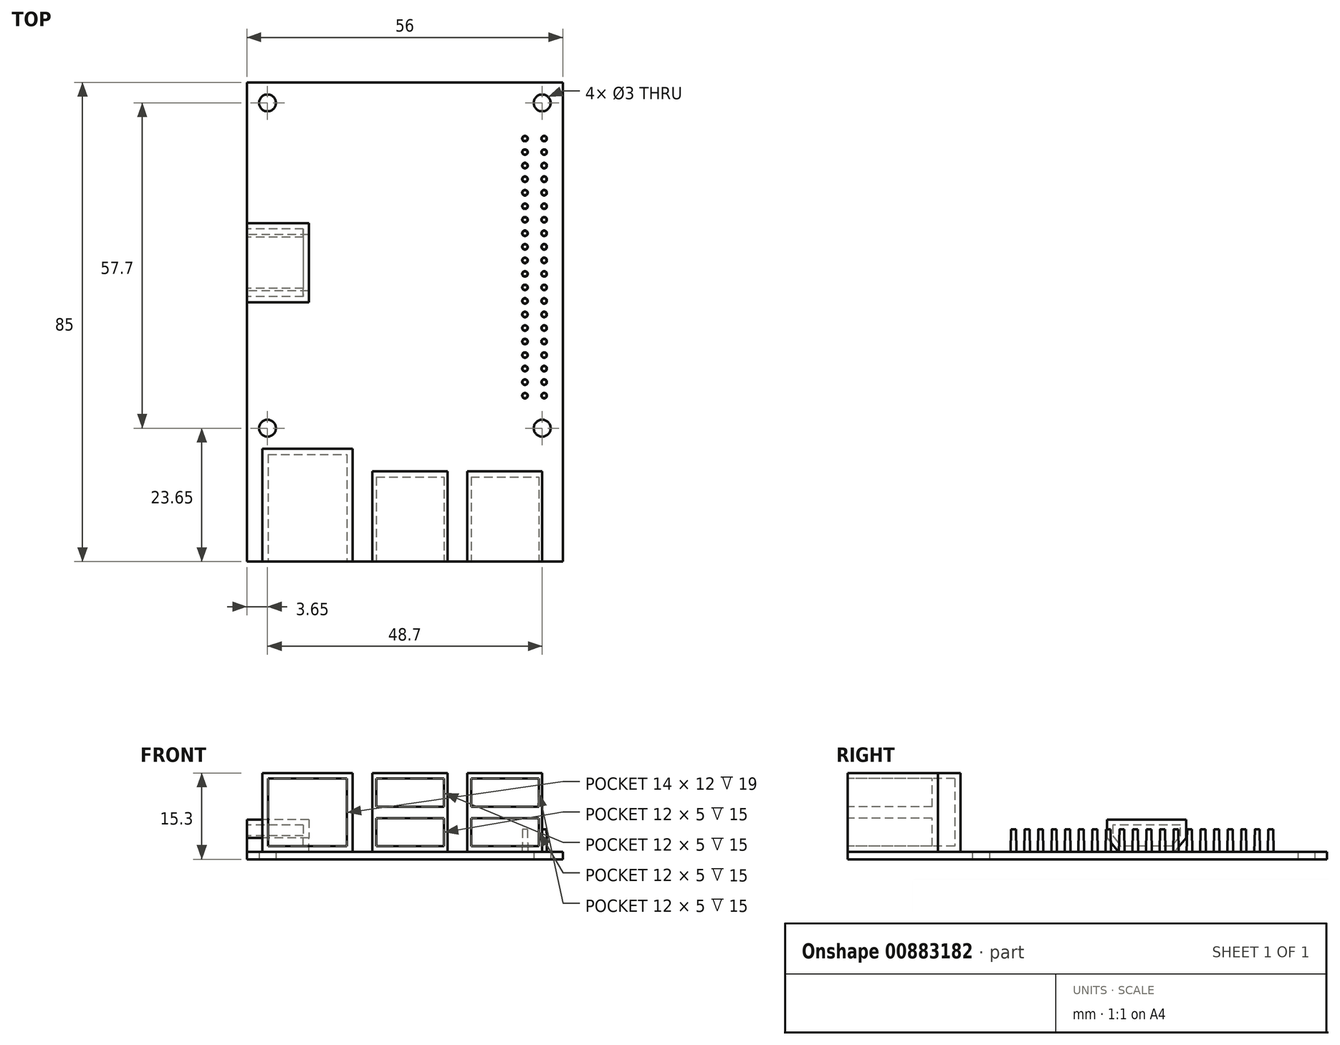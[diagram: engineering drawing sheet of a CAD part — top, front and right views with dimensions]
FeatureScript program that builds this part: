
annotation { "Feature Type Name" : "Feature", "Feature Type Description" : "" }
export const myFeature = defineFeature(function(context is Context, id is Id, definition is map)
    precondition{}
    {
        {
            var Q0;
            Q0=qCreatedBy(makeId("Top.planeOp"),FACE);
            var sketch = newSketch(context, id + "F0", { "sketchPlane" : qUnion([Q0])});
            skLineSegment(sketch, "E0.bottom", {"start": v(-28, 42.5) * mm, "end": v(28, 42.5) * mm});
            skLineSegment(sketch, "E0.top", {"start": v(-28, -42.5) * mm, "end": v(28, -42.5) * mm});
            skLineSegment(sketch, "E0.left", {"start": v(-28, 42.5) * mm, "end": v(-28, -42.5) * mm});
            skLineSegment(sketch, "E0.right", {"start": v(28, 42.5) * mm, "end": v(28, -42.5) * mm});
            skPoint(sketch, "E0.middle", {"position": v(0, 0) * mm});
            skCircle(sketch, "E1", {"center": v(-24.35, 38.85) * mm, "radius": 1.5 * mm});
            skCircle(sketch, "E2", {"center": v(-24.35, -18.85) * mm, "radius": 1.5 * mm});
            skCircle(sketch, "E3.MirrorC", {"center": v(24.35, 38.85) * mm, "radius": 1.5 * mm});
            skCircle(sketch, "E4.MirrorC", {"center": v(24.35, -18.85) * mm, "radius": 1.5 * mm});
            skSolve(sketch);
        }
        {
            var Q0;
            Q0=makeQuery(id+"F0.imprint","IMPRINT",FACE,{"disambiguationData":[TD([[makeQuery(id+"F0.imprint","IMPRINT",EDGE,{"derivedFrom":sQuery(id+"F0.wireOp",EDGE,"E0.bottom")}),-1.0]])]});
            extrude(context, id + "F1", {"entities" : qUnion([Q0]), "depth" : 1.3 * mm, "offsetDistance" : 25 * mm});
        }
        {
            var Q0;
            Q0=makeQuery(id+"F1.opExtrude","CAP_FACE",FACE,{"disambiguationData":[OSD([sQuery(id+"F0.wireOp",EDGE,"E0.bottom"),sQuery(id+"F0.wireOp",EDGE,"E0.top"),sQuery(id+"F0.wireOp",EDGE,"E0.left"),sQuery(id+"F0.wireOp",EDGE,"E0.right"),sQuery(id+"F0.wireOp",EDGE,"E1"),sQuery(id+"F0.wireOp",EDGE,"E2"),sQuery(id+"F0.wireOp",EDGE,"E3.MirrorC"),sQuery(id+"F0.wireOp",EDGE,"E4.MirrorC")])],"isStart":false});
            var sketch = newSketch(context, id + "F2", { "sketchPlane" : qUnion([Q0])});
            skLineSegment(sketch, "E5.bottom", {"start": v(-25.25, -22.5) * mm, "end": v(-9.25, -22.5) * mm});
            skLineSegment(sketch, "E5.top", {"start": v(-25.25, -43.8) * mm, "end": v(-9.25, -43.8) * mm});
            skLineSegment(sketch, "E5.left", {"start": v(-25.25, -22.5) * mm, "end": v(-25.25, -43.8) * mm});
            skLineSegment(sketch, "E5.right", {"start": v(-9.25, -22.5) * mm, "end": v(-9.25, -43.8) * mm});
            skLineSegment(sketch, "E6.bottom", {"start": v(-5.75, -26.5) * mm, "end": v(7.55, -26.5) * mm});
            skLineSegment(sketch, "E6.top", {"start": v(-5.75, -43.8) * mm, "end": v(7.55, -43.8) * mm});
            skLineSegment(sketch, "E6.left", {"start": v(-5.75, -26.5) * mm, "end": v(-5.75, -43.8) * mm});
            skLineSegment(sketch, "E6.right", {"start": v(7.55, -26.5) * mm, "end": v(7.55, -43.8) * mm});
            skLineSegment(sketch, "E7.bottom", {"start": v(11.05, -26.5) * mm, "end": v(24.35, -26.5) * mm});
            skLineSegment(sketch, "E7.top", {"start": v(11.05, -43.8) * mm, "end": v(24.35, -43.8) * mm});
            skLineSegment(sketch, "E7.left", {"start": v(11.05, -26.5) * mm, "end": v(11.05, -43.8) * mm});
            skLineSegment(sketch, "E7.right", {"start": v(24.35, -26.5) * mm, "end": v(24.35, -43.8) * mm});
            skSolve(sketch);
        }
        {
            var Q0;
            {var subQ0=sQuery(id+"F2.wireOp",EDGE,"E5.bottom");Q0=makeQuery(id+"F2.imprint","IMPRINT",FACE,{"disambiguationData":[TD([[makeQuery(id+"F2.imprint","IMPRINT",EDGE,{"derivedFrom":subQ0}),-1.0]])]});}
            var Q1;
            {var subQ0=sQuery(id+"F2.wireOp",EDGE,"E6.bottom");Q1=makeQuery(id+"F2.imprint","IMPRINT",FACE,{"disambiguationData":[TD([[makeQuery(id+"F2.imprint","IMPRINT",EDGE,{"derivedFrom":subQ0}),-1.0]])]});}
            var Q2;
            {var subQ0=sQuery(id+"F2.wireOp",EDGE,"E7.bottom");Q2=makeQuery(id+"F2.imprint","IMPRINT",FACE,{"disambiguationData":[TD([[makeQuery(id+"F2.imprint","IMPRINT",EDGE,{"derivedFrom":subQ0}),-1.0]])]});}
            extrude(context, id + "F3", {"entities" : qUnion([Q0, Q1, Q2]), "depth" : 14 * mm, "offsetDistance" : 25 * mm});
        }
        {
            var Q0;
            {var subQ0=sQuery(id+"F0.wireOp",EDGE,"E0.top");var subQ1=makeQuery(id+"F1.opExtrude","CAP_EDGE",EDGE,{"disambiguationData":[OSD([subQ0])],"isStart":false});Q0=makeQuery(id+"F3.opExtrude","SWEPT_FACE",FACE,{"disambiguationData":[OSD([subQ0]),TDD([makeQuery(id+"F2.imprint","IMPRINT",EDGE,{"disambiguationData":[TD([[makeQuery(id+"F2.imprint","INTERSECT",VERTEX,{"derivedFrom":[subQ1,sQuery(id+"F2.wireOp",EDGE,"E5.left")]}),-1.0]])],"derivedFrom":subQ1})])]});}
            shell(context, id + "F4", {"entities" : qUnion([Q0]), "thickness" : 1 * mm});
        }
        {
            var Q0;
            {var subQ0=sQuery(id+"F0.wireOp",EDGE,"E0.top");var subQ1=makeQuery(id+"F1.opExtrude","CAP_EDGE",EDGE,{"disambiguationData":[OSD([subQ0])],"isStart":false});Q0=makeQuery(id+"F3.opExtrude","SWEPT_FACE",FACE,{"disambiguationData":[OSD([subQ0]),TDD([makeQuery(id+"F2.imprint","IMPRINT",EDGE,{"disambiguationData":[TD([[makeQuery(id+"F2.imprint","INTERSECT",VERTEX,{"derivedFrom":[subQ1,sQuery(id+"F2.wireOp",EDGE,"E6.left")]}),-1.0]])],"derivedFrom":subQ1})])]});}
            var sketch = newSketch(context, id + "F5", { "sketchPlane" : qUnion([Q0])});
            skLineSegment(sketch, "E8.bottom", {"start": v(-5.05, 9.3) * mm, "end": v(6.95, 9.3) * mm});
            skLineSegment(sketch, "E8.top", {"start": v(-5.05, 14.3) * mm, "end": v(6.95, 14.3) * mm});
            skLineSegment(sketch, "E8.left", {"start": v(-5.05, 9.3) * mm, "end": v(-5.05, 14.3) * mm});
            skLineSegment(sketch, "E8.right", {"start": v(6.95, 9.3) * mm, "end": v(6.95, 14.3) * mm});
            skLineSegment(sketch, "E9.bottom", {"start": v(-5.05, 2.3) * mm, "end": v(6.95, 2.3) * mm});
            skLineSegment(sketch, "E9.top", {"start": v(-5.05, 7.3) * mm, "end": v(6.95, 7.3) * mm});
            skLineSegment(sketch, "E9.left", {"start": v(-5.05, 2.3) * mm, "end": v(-5.05, 7.3) * mm});
            skLineSegment(sketch, "E9.right", {"start": v(6.95, 2.3) * mm, "end": v(6.95, 7.3) * mm});
            skLineSegment(sketch, "E10.bottom", {"start": v(11.75, 9.3) * mm, "end": v(23.75, 9.3) * mm});
            skLineSegment(sketch, "E10.top", {"start": v(11.75, 14.3) * mm, "end": v(23.75, 14.3) * mm});
            skLineSegment(sketch, "E10.left", {"start": v(11.75, 9.3) * mm, "end": v(11.75, 14.3) * mm});
            skLineSegment(sketch, "E10.right", {"start": v(23.75, 9.3) * mm, "end": v(23.75, 14.3) * mm});
            skLineSegment(sketch, "E11.bottom", {"start": v(11.75, 2.3) * mm, "end": v(23.75, 2.3) * mm});
            skLineSegment(sketch, "E11.top", {"start": v(11.75, 7.3) * mm, "end": v(23.75, 7.3) * mm});
            skLineSegment(sketch, "E11.left", {"start": v(11.75, 2.3) * mm, "end": v(11.75, 7.3) * mm});
            skLineSegment(sketch, "E11.right", {"start": v(23.75, 2.3) * mm, "end": v(23.75, 7.3) * mm});
            skSolve(sketch);
        }
        {
            var Q0;
            Q0 = qSketchRegion(id + "F5", true);
            extrude(context, id + "F6", {"entities" : qUnion([Q0]), "operationType" : NewBodyOperationType.REMOVE, "endBound" : BoundingType.UP_TO_NEXT, "oppositeDirection" : true, "depth" : 25 * mm, "hasOffset" : true, "offsetDistance" : 1 * mm});
        }
        {
            var Q0;
            Q0=makeQuery(id+"F1.opExtrude","SWEPT_FACE",FACE,{"disambiguationData":[OSD([sQuery(id+"F0.wireOp",EDGE,"E0.left")])]});
            var sketch = newSketch(context, id + "F7", { "sketchPlane" : qUnion([Q0])});
            skLineSegment(sketch, "E12", {"start": v(-15.5, 1.3) * mm, "end": v(-17.5, 3.8) * mm});
            skLineSegment(sketch, "E13", {"start": v(-17.5, 3.8) * mm, "end": v(-17.5, 7.05) * mm});
            skLineSegment(sketch, "E14", {"start": v(-17.5, 7.05) * mm, "end": v(-3.5, 7.05) * mm});
            skLineSegment(sketch, "E15", {"start": v(-3.5, 7.05) * mm, "end": v(-3.5, 3.8) * mm});
            skLineSegment(sketch, "E16", {"start": v(-3.5, 3.8) * mm, "end": v(-5.5, 1.3) * mm});
            skLineSegment(sketch, "E17", {"start": v(-5.5, 1.3) * mm, "end": v(-15.5, 1.3) * mm});
            skSolve(sketch);
        }
        {
            var Q0;
            Q0=makeQuery(id+"F7.imprint","IMPRINT",FACE,{"disambiguationData":[TD([[makeQuery(id+"F7.imprint","IMPRINT",EDGE,{"derivedFrom":sQuery(id+"F7.wireOp",EDGE,"E12")}),-1.0]])]});
            extrude(context, id + "F8", {"entities" : qUnion([Q0]), "oppositeDirection" : true, "depth" : 11 * mm, "offsetDistance" : 25 * mm});
        }
        {
            var Q0;
            Q0=makeQuery(id+"F8.opExtrude","CAP_FACE",FACE,{"disambiguationData":[OSD([sQuery(id+"F7.wireOp",EDGE,"E12"),sQuery(id+"F7.wireOp",EDGE,"E13"),sQuery(id+"F7.wireOp",EDGE,"E14"),sQuery(id+"F7.wireOp",EDGE,"E15"),sQuery(id+"F7.wireOp",EDGE,"E16"),sQuery(id+"F7.wireOp",EDGE,"E17")])],"isStart":true});
            shell(context, id + "F9", {"entities" : qUnion([Q0]), "thickness" : 1 * mm});
        }
        {
            var Q0;
            Q0=makeQuery(id+"F1.opExtrude","CAP_FACE",FACE,{"disambiguationData":[OSD([sQuery(id+"F0.wireOp",EDGE,"E0.bottom"),sQuery(id+"F0.wireOp",EDGE,"E0.top"),sQuery(id+"F0.wireOp",EDGE,"E0.left"),sQuery(id+"F0.wireOp",EDGE,"E0.right"),sQuery(id+"F0.wireOp",EDGE,"E1"),sQuery(id+"F0.wireOp",EDGE,"E2"),sQuery(id+"F0.wireOp",EDGE,"E3.MirrorC"),sQuery(id+"F0.wireOp",EDGE,"E4.MirrorC")])],"isStart":false});
            var sketch = newSketch(context, id + "F10", { "sketchPlane" : qUnion([Q0])});
            skCircle(sketch, "E18", {"center": v(21.3, 32.52) * mm, "radius": 0.5 * mm});
            skCircle(sketch, "E19.0.1.0", {"center": v(21.3, 30.12) * mm, "radius": 0.5 * mm});
            skCircle(sketch, "E19.0.2.0", {"center": v(21.3, 27.72) * mm, "radius": 0.5 * mm});
            skCircle(sketch, "E19.0.3.0", {"center": v(21.3, 25.32) * mm, "radius": 0.5 * mm});
            skCircle(sketch, "E19.0.4.0", {"center": v(21.3, 22.92) * mm, "radius": 0.5 * mm});
            skCircle(sketch, "E19.0.5.0", {"center": v(21.3, 20.52) * mm, "radius": 0.5 * mm});
            skCircle(sketch, "E19.0.6.0", {"center": v(21.3, 18.12) * mm, "radius": 0.5 * mm});
            skCircle(sketch, "E19.0.7.0", {"center": v(21.3, 15.72) * mm, "radius": 0.5 * mm});
            skCircle(sketch, "E19.0.8.0", {"center": v(21.3, 13.32) * mm, "radius": 0.5 * mm});
            skCircle(sketch, "E19.0.9.0", {"center": v(21.3, 10.92) * mm, "radius": 0.5 * mm});
            skCircle(sketch, "E19.0.10.0", {"center": v(21.3, 8.52) * mm, "radius": 0.5 * mm});
            skCircle(sketch, "E19.0.11.0", {"center": v(21.3, 6.12) * mm, "radius": 0.5 * mm});
            skCircle(sketch, "E19.0.12.0", {"center": v(21.3, 3.72) * mm, "radius": 0.5 * mm});
            skCircle(sketch, "E19.0.13.0", {"center": v(21.3, 1.32) * mm, "radius": 0.5 * mm});
            skCircle(sketch, "E19.0.14.0", {"center": v(21.3, -1.08) * mm, "radius": 0.5 * mm});
            skCircle(sketch, "E19.0.15.0", {"center": v(21.3, -3.48) * mm, "radius": 0.5 * mm});
            skCircle(sketch, "E19.0.16.0", {"center": v(21.3, -5.88) * mm, "radius": 0.5 * mm});
            skCircle(sketch, "E19.0.17.0", {"center": v(21.3, -8.28) * mm, "radius": 0.5 * mm});
            skCircle(sketch, "E19.0.18.0", {"center": v(21.3, -10.68) * mm, "radius": 0.5 * mm});
            skCircle(sketch, "E19.0.19.0", {"center": v(21.3, -13.08) * mm, "radius": 0.5 * mm});
            skCircle(sketch, "E19.1.0.0", {"center": v(24.7, 32.52) * mm, "radius": 0.5 * mm});
            skCircle(sketch, "E19.1.1.0", {"center": v(24.7, 30.12) * mm, "radius": 0.5 * mm});
            skCircle(sketch, "E19.1.2.0", {"center": v(24.7, 27.72) * mm, "radius": 0.5 * mm});
            skCircle(sketch, "E19.1.3.0", {"center": v(24.7, 25.32) * mm, "radius": 0.5 * mm});
            skCircle(sketch, "E19.1.4.0", {"center": v(24.7, 22.92) * mm, "radius": 0.5 * mm});
            skCircle(sketch, "E19.1.5.0", {"center": v(24.7, 20.52) * mm, "radius": 0.5 * mm});
            skCircle(sketch, "E19.1.6.0", {"center": v(24.7, 18.12) * mm, "radius": 0.5 * mm});
            skCircle(sketch, "E19.1.7.0", {"center": v(24.7, 15.72) * mm, "radius": 0.5 * mm});
            skCircle(sketch, "E19.1.8.0", {"center": v(24.7, 13.32) * mm, "radius": 0.5 * mm});
            skCircle(sketch, "E19.1.9.0", {"center": v(24.7, 10.92) * mm, "radius": 0.5 * mm});
            skCircle(sketch, "E19.1.10.0", {"center": v(24.7, 8.52) * mm, "radius": 0.5 * mm});
            skCircle(sketch, "E19.1.11.0", {"center": v(24.7, 6.12) * mm, "radius": 0.5 * mm});
            skCircle(sketch, "E19.1.12.0", {"center": v(24.7, 3.72) * mm, "radius": 0.5 * mm});
            skCircle(sketch, "E19.1.13.0", {"center": v(24.7, 1.32) * mm, "radius": 0.5 * mm});
            skCircle(sketch, "E19.1.14.0", {"center": v(24.7, -1.08) * mm, "radius": 0.5 * mm});
            skCircle(sketch, "E19.1.15.0", {"center": v(24.7, -3.48) * mm, "radius": 0.5 * mm});
            skCircle(sketch, "E19.1.16.0", {"center": v(24.7, -5.88) * mm, "radius": 0.5 * mm});
            skCircle(sketch, "E19.1.17.0", {"center": v(24.7, -8.28) * mm, "radius": 0.5 * mm});
            skCircle(sketch, "E19.1.18.0", {"center": v(24.7, -10.68) * mm, "radius": 0.5 * mm});
            skCircle(sketch, "E19.1.19.0", {"center": v(24.7, -13.08) * mm, "radius": 0.5 * mm});
            skLineSegment(sketch, "E19.direction1", {"start": v(21.3, 32.52) * mm, "end": v(24.7, 32.52) * mm, "construction": true});
            skLineSegment(sketch, "E19.direction2", {"start": v(21.3, 32.52) * mm, "end": v(21.3, 30.12) * mm, "construction": true});
            skSolve(sketch);
        }
        {
            var Q0;
            Q0 = qSketchRegion(id + "F10", true);
            extrude(context, id + "F11", {"entities" : qUnion([Q0]), "depth" : 4 * mm, "offsetDistance" : 25 * mm, "hasDraft" : true, "draftAngle" : 1 * degree, "draftPullDirection" : true});
        }
    });
